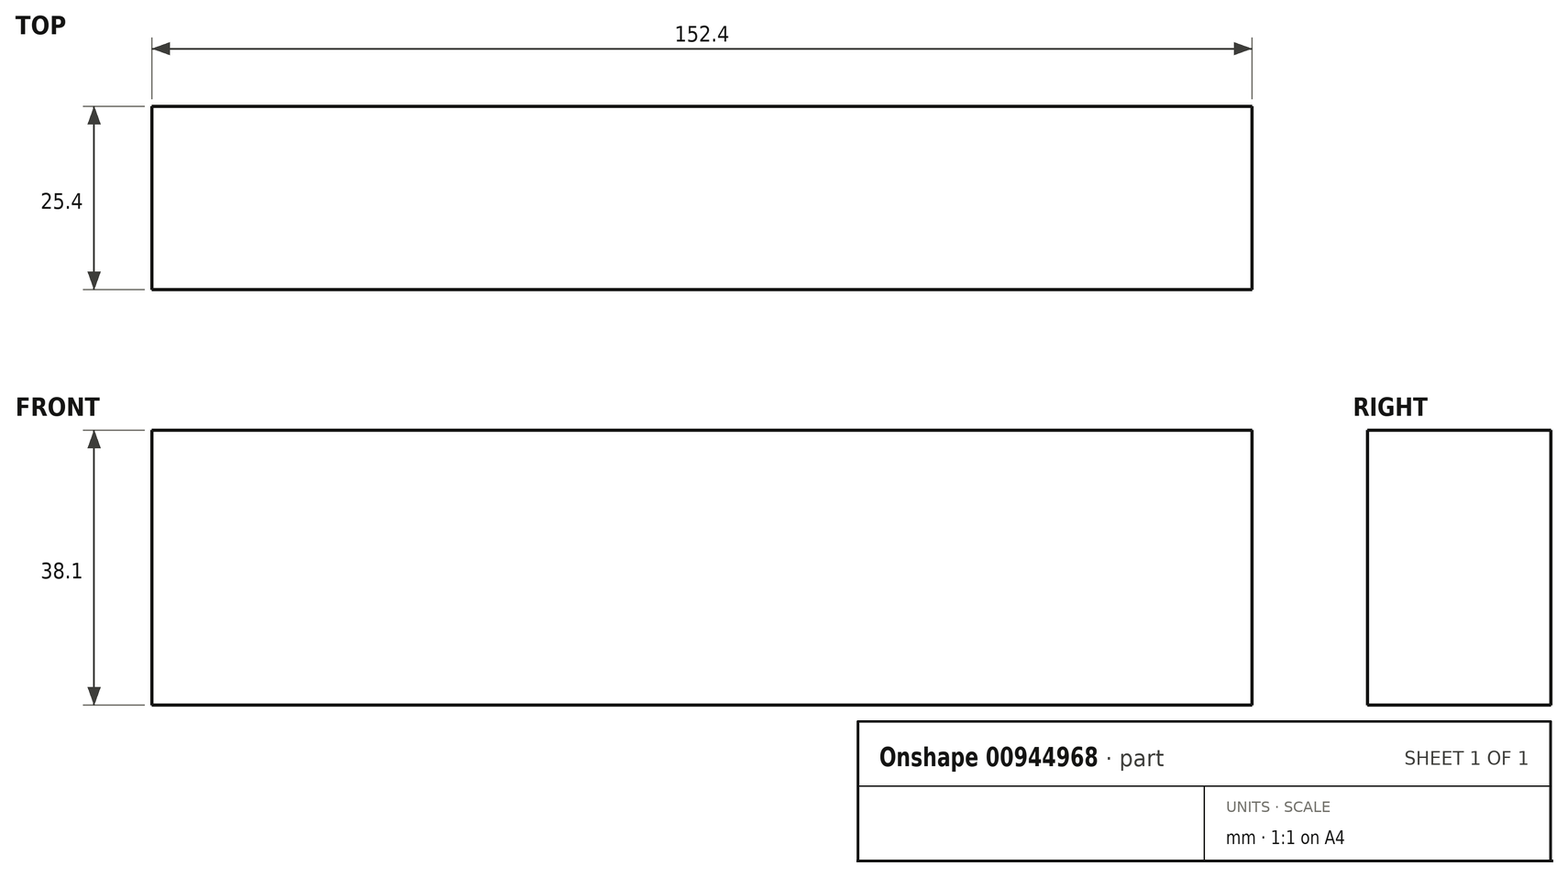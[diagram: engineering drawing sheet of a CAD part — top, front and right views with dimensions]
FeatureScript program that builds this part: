
annotation { "Feature Type Name" : "Feature", "Feature Type Description" : "" }
export const myFeature = defineFeature(function(context is Context, id is Id, definition is map)
    precondition{}
    {
        {
            var Q0;
            Q0=qCreatedBy(makeId("Front.planeOp"),FACE);
            var sketch = newSketch(context, id + "F0", { "sketchPlane" : qUnion([Q0])});
            skLineSegment(sketch, "E0.bottom", {"start": v(0, 0) * mm, "end": v(152.4, 0) * mm});
            skLineSegment(sketch, "E0.top", {"start": v(0, 38.1) * mm, "end": v(152.4, 38.1) * mm});
            skLineSegment(sketch, "E0.left", {"start": v(0, 0) * mm, "end": v(0, 38.1) * mm});
            skLineSegment(sketch, "E0.right", {"start": v(152.4, 0) * mm, "end": v(152.4, 38.1) * mm});
            skSolve(sketch);
        }
        {
            var Q0;
            Q0=makeQuery(id+"F0.imprint","IMPRINT",FACE,{"disambiguationData":[TD([[makeQuery(id+"F0.imprint","IMPRINT",EDGE,{"derivedFrom":sQuery(id+"F0.wireOp",EDGE,"E0.bottom")}),1.0]])]});
            extrude(context, id + "F1", {"entities" : qUnion([Q0]), "oppositeDirection" : true, "depth" : 25.4 * mm, "offsetDistance" : 25.4 * mm});
        }
    });
